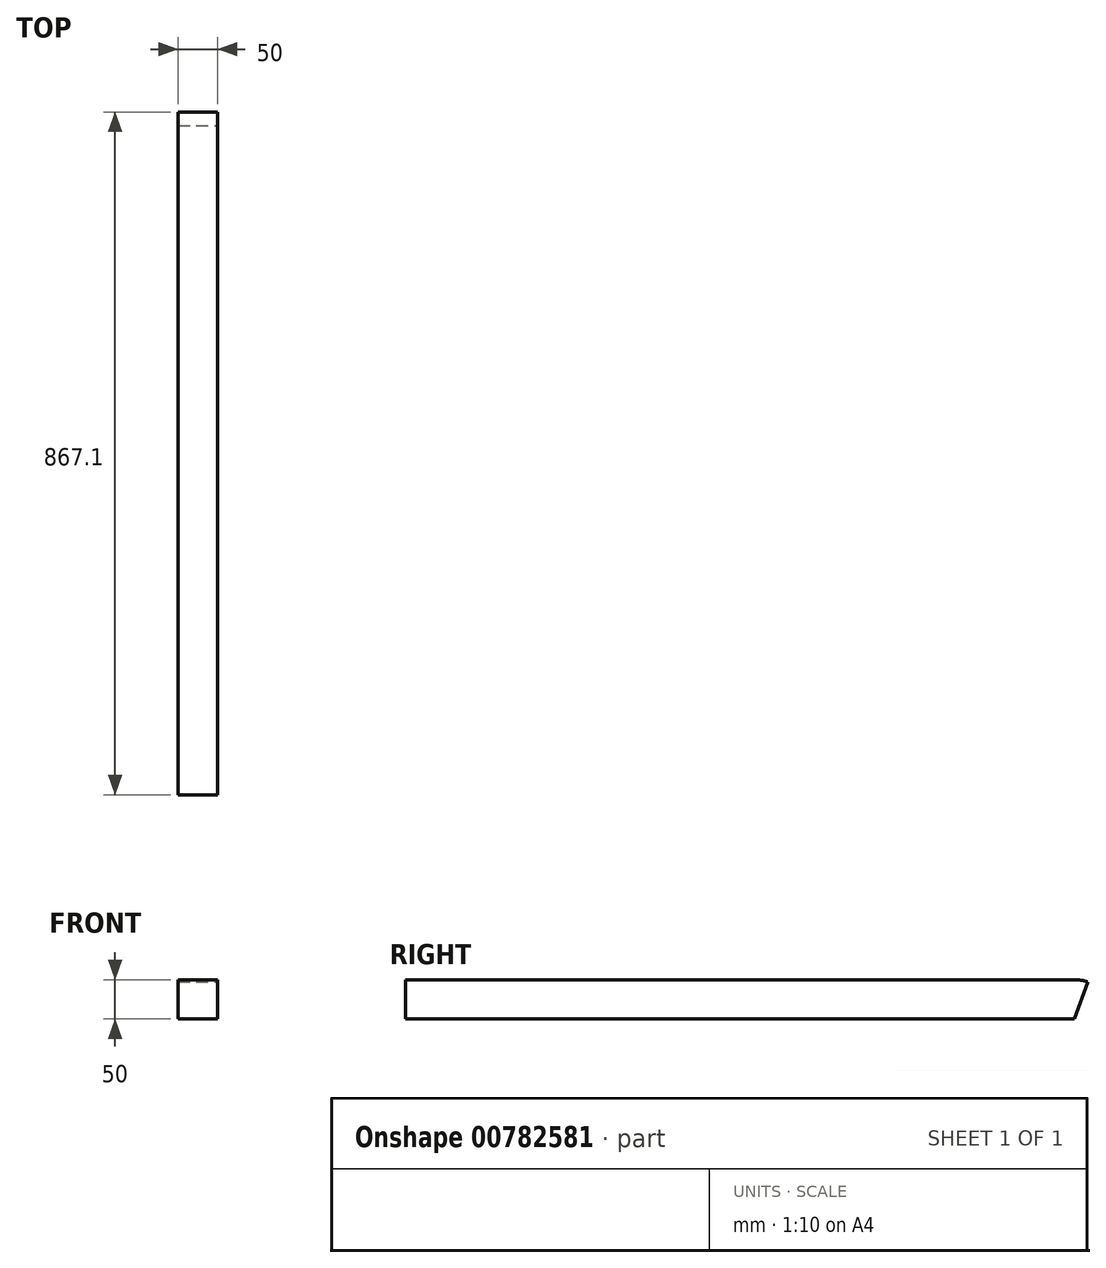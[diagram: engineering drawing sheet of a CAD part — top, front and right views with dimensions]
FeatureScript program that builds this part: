
annotation { "Feature Type Name" : "Feature", "Feature Type Description" : "" }
export const myFeature = defineFeature(function(context is Context, id is Id, definition is map)
    precondition{}
    {
        {
            var Q0;
            Q0=qCreatedBy(makeId("Front.planeOp"),FACE);
            var sketch = newSketch(context, id + "F0", { "sketchPlane" : qUnion([Q0])});
            skLineSegment(sketch, "E0.bottom", {"start": v(0, 0) * mm, "end": v(50, 0) * mm});
            skLineSegment(sketch, "E0.top", {"start": v(0, 50) * mm, "end": v(50, 50) * mm});
            skLineSegment(sketch, "E0.left", {"start": v(0, 0) * mm, "end": v(0, 50) * mm});
            skLineSegment(sketch, "E0.right", {"start": v(50, 0) * mm, "end": v(50, 50) * mm});
            skSolve(sketch);
        }
        {
            var Q0;
            Q0=qSketchRegion(id+"F0",true);
            extrude(context, id + "F1", {"entities" : qUnion([Q0]), "depth" : 850 * mm, "offsetDistance" : 25 * mm});
        }
        {
            var Q0;
            Q0=qCreatedBy(makeId("Front.planeOp"),FACE);
            var sketch = newSketch(context, id + "F2", { "sketchPlane" : qUnion([Q0])});
            skLineSegment(sketch, "E1.bottom", {"start": v(0, 0) * mm, "end": v(50, 0) * mm});
            skLineSegment(sketch, "E1.top", {"start": v(0, 50) * mm, "end": v(50, 50) * mm});
            skLineSegment(sketch, "E1.left", {"start": v(0, 0) * mm, "end": v(0, 50) * mm});
            skLineSegment(sketch, "E1.right", {"start": v(50, 0) * mm, "end": v(50, 50) * mm});
            skSolve(sketch);
        }
        {
            var Q0;
            Q0=makeQuery(id+"F2.imprint","IMPRINT",FACE,{"disambiguationData":[TD([[makeQuery(id+"F2.imprint","IMPRINT",EDGE,{"derivedFrom":sQuery(id+"F2.wireOp",EDGE,"E1.bottom")}),1.0]])]});
            var Q1;
            Q1=sQuery(id+"F2.wireOp",EDGE,"E1.bottom");
            revolve(context, id + "F3", {"operationType" : NewBodyOperationType.ADD, "surfaceOperationType" : NewSurfaceOperationType.NEW, "entities" : qUnion([Q0]), "axis" : qUnion([Q1]), "revolveType" : RevolveType.ONE_DIRECTION, "oppositeDirection" : true, "angle" : 20 * degree});
        }
    });
